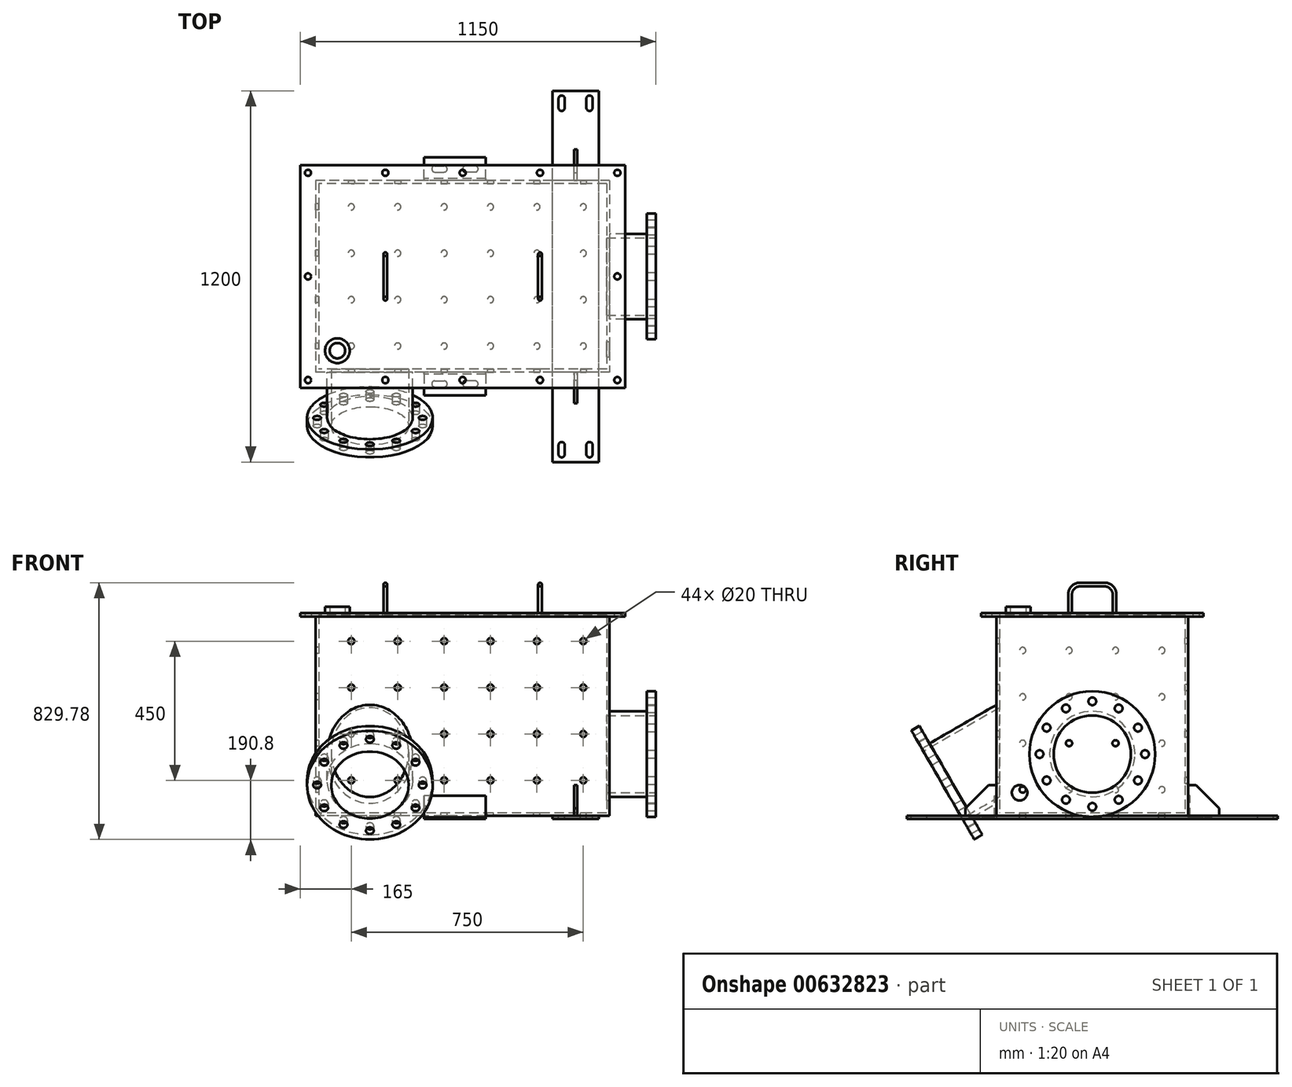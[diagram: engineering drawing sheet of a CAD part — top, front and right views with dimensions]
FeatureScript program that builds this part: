
annotation { "Feature Type Name" : "Feature", "Feature Type Description" : "" }
export const myFeature = defineFeature(function(context is Context, id is Id, definition is map)
    precondition{}
    {
        {
            var Q0;
            Q0=qCreatedBy(makeId("Top.planeOp"),FACE);
            var sketch = newSketch(context, id + "F0", { "sketchPlane" : qUnion([Q0])});
            skLineSegment(sketch, "E0.bottom", {"start": v(475, 310) * mm, "end": v(-475, 310) * mm});
            skLineSegment(sketch, "E0.top", {"start": v(475, -310) * mm, "end": v(-475, -310) * mm});
            skLineSegment(sketch, "E0.left", {"start": v(475, 310) * mm, "end": v(475, -310) * mm});
            skLineSegment(sketch, "E0.right", {"start": v(-475, 310) * mm, "end": v(-475, -310) * mm});
            skPoint(sketch, "E0.middle", {"position": v(0, 0) * mm});
            skSolve(sketch);
        }
        {
            var Q0;
            Q0=makeQuery(id+"F0.imprint","IMPRINT",FACE,{"disambiguationData":[TD([[makeQuery(id+"F0.imprint","IMPRINT",EDGE,{"derivedFrom":sQuery(id+"F0.wireOp",EDGE,"E0.bottom")}),1.0]])]});
            extrude(context, id + "F1", {"entities" : qUnion([Q0]), "depth" : 650 * mm, "offsetDistance" : 25 * mm});
        }
        {
            var Q0;
            Q0=makeQuery(id+"F1.opExtrude","CAP_FACE",FACE,{"disambiguationData":[OSD([sQuery(id+"F0.wireOp",EDGE,"E0.bottom"),sQuery(id+"F0.wireOp",EDGE,"E0.top"),sQuery(id+"F0.wireOp",EDGE,"E0.left"),sQuery(id+"F0.wireOp",EDGE,"E0.right")])],"isStart":false});
            var Q1;
            Q1=makeQuery(id+"F1.opExtrude","SWEPT_BODY",BODY,{"disambiguationData":[OSD([sQuery(id+"F0.wireOp",EDGE,"E0.bottom"),sQuery(id+"F0.wireOp",EDGE,"E0.top"),sQuery(id+"F0.wireOp",EDGE,"E0.left"),sQuery(id+"F0.wireOp",EDGE,"E0.right")])]});
            shell(context, id + "F2", {"entities" : qUnion([Q0]), "parts" : qUnion([Q1]), "thickness" : 10 * mm});
        }
        {
            var Q0;
            Q0=makeQuery(id+"F1.opExtrude","SWEPT_FACE",FACE,{"disambiguationData":[OSD([sQuery(id+"F0.wireOp",EDGE,"E0.left")])]});
            var sketch = newSketch(context, id + "F3", { "sketchPlane" : qUnion([Q0])});
            skCircle(sketch, "E1", {"center": v(0, 200) * mm, "radius": 125 * mm});
            skLineSegment(sketch, "E2", {"start": v(0, 0) * mm, "end": v(0, 200) * mm, "construction": true});
            skSolve(sketch);
        }
        {
            var Q0;
            Q0=sQuery(id+"F3.wireOp",VERTEX,"E1.center");
            var Q1;
            Q1=makeQuery(id+"F1.opExtrude","SWEPT_BODY",BODY,{"disambiguationData":[OSD([sQuery(id+"F0.wireOp",EDGE,"E0.bottom"),sQuery(id+"F0.wireOp",EDGE,"E0.top"),sQuery(id+"F0.wireOp",EDGE,"E0.left"),sQuery(id+"F0.wireOp",EDGE,"E0.right")])]});
            hole(context, id + "F4", {"style" : HoleStyle.SIMPLE, "endStyle" : HoleEndStyle.BLIND, "holeDiameter" : 250 * mm, "majorDiameter" : 5 * mm, "holeDepth" : 200 * mm, "isTappedThrough" : true, "tappedDepth" : 12 * mm, "tapClearance" : 3, "locations" : qUnion([Q0]), "scope" : qUnion([Q1])});
        }
        {
            var Q0;
            Q0=makeQuery(id+"F1.opExtrude","SWEPT_FACE",FACE,{"disambiguationData":[OSD([sQuery(id+"F0.wireOp",EDGE,"E0.top")])]});
            var sketch = newSketch(context, id + "F5", { "sketchPlane" : qUnion([Q0])});
            skCircle(sketch, "E3", {"center": v(-300, 200) * mm, "radius": 125 * mm});
            skLineSegment(sketch, "E4", {"start": v(-425, 200) * mm, "end": v(-175, 200) * mm, "construction": true});
            skSolve(sketch);
        }
        {
            var Q0;
            Q0=makeQuery(id+"F1.opExtrude","CAP_FACE",FACE,{"disambiguationData":[OSD([sQuery(id+"F0.wireOp",EDGE,"E0.bottom"),sQuery(id+"F0.wireOp",EDGE,"E0.top"),sQuery(id+"F0.wireOp",EDGE,"E0.left"),sQuery(id+"F0.wireOp",EDGE,"E0.right")])],"isStart":false});
            var sketch = newSketch(context, id + "F6", { "sketchPlane" : qUnion([Q0])});
            skLineSegment(sketch, "E5.bottom", {"start": v(475, 310) * mm, "end": v(-475, 310) * mm});
            skLineSegment(sketch, "E5.top", {"start": v(475, -310) * mm, "end": v(-475, -310) * mm});
            skLineSegment(sketch, "E5.left", {"start": v(475, 310) * mm, "end": v(475, -310) * mm});
            skLineSegment(sketch, "E5.right", {"start": v(-475, 310) * mm, "end": v(-475, -310) * mm});
            skPoint(sketch, "E5.middle", {"position": v(0, 0) * mm});
            skLineSegment(sketch, "E6.bottom", {"start": v(525, 360) * mm, "end": v(-525, 360) * mm});
            skLineSegment(sketch, "E6.top", {"start": v(525, -360) * mm, "end": v(-525, -360) * mm});
            skLineSegment(sketch, "E6.left", {"start": v(525, 360) * mm, "end": v(525, -360) * mm});
            skLineSegment(sketch, "E6.right", {"start": v(-525, 360) * mm, "end": v(-525, -360) * mm});
            skSolve(sketch);
        }
        {
            var Q0;
            Q0=makeQuery(id+"F6.imprint","IMPRINT",FACE,{"disambiguationData":[TD([[makeQuery(id+"F6.imprint","IMPRINT",EDGE,{"derivedFrom":sQuery(id+"F6.wireOp",EDGE,"E5.bottom")}),-1.0]])]});
            var sketch = newSketch(context, id + "F7", { "sketchPlane" : qUnion([Q0])});
            skCircle(sketch, "E7", {"center": v(-500, 335) * mm, "radius": 10 * mm});
            skCircle(sketch, "E8.MirrorC", {"center": v(500, 335) * mm, "radius": 10 * mm});
            skCircle(sketch, "E9", {"center": v(0, 335) * mm, "radius": 10 * mm});
            skCircle(sketch, "E10", {"center": v(250, 335) * mm, "radius": 10 * mm});
            skCircle(sketch, "E11", {"center": v(-250, 335) * mm, "radius": 10 * mm});
            skCircle(sketch, "E12", {"center": v(-500, 0) * mm, "radius": 10 * mm});
            skCircle(sketch, "E13", {"center": v(500, 0) * mm, "radius": 10 * mm});
            skCircle(sketch, "E14.MirrorC", {"center": v(-250, -335) * mm, "radius": 10 * mm});
            skCircle(sketch, "E15.MirrorC", {"center": v(0, -335) * mm, "radius": 10 * mm});
            skCircle(sketch, "E16.MirrorC", {"center": v(250, -335) * mm, "radius": 10 * mm});
            skCircle(sketch, "E17.MirrorC", {"center": v(500, -335) * mm, "radius": 10 * mm});
            skCircle(sketch, "E18.MirrorC", {"center": v(-500, -335) * mm, "radius": 10 * mm});
            skSolve(sketch);
        }
        {
            var Q0;
            Q0=makeQuery(id+"FEyW0m5oHBMubmV_1.boolean.opBoolean","MERGE",FACE,{"derivedFrom":[makeQuery(id+"Fs8Oh72M1rwnpf4_1.boolean.opBoolean","MERGE",FACE,{"derivedFrom":[makeQuery(id+"F1.opExtrude","SWEPT_FACE",FACE,{"disambiguationData":[OSD([sQuery(id+"F0.wireOp",EDGE,"E0.left")])]}),makeQuery(id+"Fs8Oh72M1rwnpf4_1.opExtrude","SWEPT_FACE",FACE,{"disambiguationData":[OSD([sQuery(id+"F4QqQAWiacnO0fX_1.wireOp",EDGE,"CHtHYlyW-yg5j-FexC-awxB-8z9hYpKb7upd.right")])]})]}),makeQuery(id+"FEyW0m5oHBMubmV_1.opExtrude","SWEPT_FACE",FACE,{"disambiguationData":[OSD([sQuery(id+"F0J5bgxU2wIGMiN_1.wireOp",EDGE,"msL39oIi-AbLE-4iKB-2RcJ-U97ccpWqk1Ai.left")])]})]});
            var sketch = newSketch(context, id + "F8", { "sketchPlane" : qUnion([Q0])});
            skCircle(sketch, "E19", {"center": v(0, 200) * mm, "radius": 138 * mm});
            skSolve(sketch);
        }
        {
            var Q0;
            Q0=makeQuery(id+"F8.imprint","IMPRINT",FACE,{"disambiguationData":[TD([[makeQuery(id+"F8.imprint","IMPRINT",EDGE,{"derivedFrom":sQuery(id+"F8.wireOp",EDGE,"E19")}),1.0]])]});
            extrude(context, id + "F9", {"entities" : qUnion([Q0]), "operationType" : NewBodyOperationType.ADD, "depth" : 150 * mm, "offsetDistance" : 25 * mm});
        }
        {
            var Q0;
            Q0=makeQuery(id+"F9.opExtrude","CAP_FACE",FACE,{"disambiguationData":[OSD([sQuery(id+"F4.hole-0.sketch.wireOp",EDGE,"core_line_2"),sQuery(id+"F4.hole-0.sketch.wireOp",EDGE,"core_line_3"),sQuery(id+"F8.wireOp",EDGE,"E19")])],"isStart":false});
            var sketch = newSketch(context, id + "F10", { "sketchPlane" : qUnion([Q0])});
            skCircle(sketch, "E20", {"center": v(0, 200) * mm, "radius": 203 * mm});
            skCircle(sketch, "E21", {"center": v(0, 370.5) * mm, "radius": 12.5 * mm});
            skCircle(sketch, "E22.1.0", {"center": v(-85.25, 347.66) * mm, "radius": 12.5 * mm});
            skCircle(sketch, "E22.2.0", {"center": v(-147.66, 285.25) * mm, "radius": 12.5 * mm});
            skCircle(sketch, "E22.3.0", {"center": v(-170.5, 200) * mm, "radius": 12.5 * mm});
            skCircle(sketch, "E22.4.0", {"center": v(-147.66, 114.75) * mm, "radius": 12.5 * mm});
            skCircle(sketch, "E22.5.0", {"center": v(-85.25, 52.34) * mm, "radius": 12.5 * mm});
            skCircle(sketch, "E22.6.0", {"center": v(0, 29.5) * mm, "radius": 12.5 * mm});
            skCircle(sketch, "E22.7.0", {"center": v(85.25, 52.34) * mm, "radius": 12.5 * mm});
            skCircle(sketch, "E22.8.0", {"center": v(147.66, 114.75) * mm, "radius": 12.5 * mm});
            skCircle(sketch, "E22.9.0", {"center": v(170.5, 200) * mm, "radius": 12.5 * mm});
            skCircle(sketch, "E22.10.0", {"center": v(147.66, 285.25) * mm, "radius": 12.5 * mm});
            skCircle(sketch, "E22.11.0", {"center": v(85.25, 347.66) * mm, "radius": 12.5 * mm});
            skCircle(sketch, "E23", {"center": v(0, 200) * mm, "radius": 170.5 * mm, "construction": true});
            skSolve(sketch);
        }
        {
            var Q0;
            Q0=makeQuery(id+"F10.imprint","IMPRINT",FACE,{"disambiguationData":[TD([[makeQuery(id+"F10.imprint","IMPRINT",EDGE,{"derivedFrom":sQuery(id+"F10.wireOp",EDGE,"E20")}),1.0]])]});
            extrude(context, id + "F11", {"entities" : qUnion([Q0]), "operationType" : NewBodyOperationType.ADD, "oppositeDirection" : true, "depth" : 30 * mm, "hasOffset" : true, "offsetDistance" : 30 * mm});
        }
        {
            var Q0;
            Q0=makeQuery(id+"FEyW0m5oHBMubmV_1.boolean.opBoolean","MERGE",FACE,{"derivedFrom":[makeQuery(id+"Fs8Oh72M1rwnpf4_1.boolean.opBoolean","MERGE",FACE,{"derivedFrom":[makeQuery(id+"F1.opExtrude","SWEPT_FACE",FACE,{"disambiguationData":[OSD([sQuery(id+"F0.wireOp",EDGE,"E0.right")])]}),makeQuery(id+"Fs8Oh72M1rwnpf4_1.opExtrude","SWEPT_FACE",FACE,{"disambiguationData":[OSD([sQuery(id+"F4QqQAWiacnO0fX_1.wireOp",EDGE,"CHtHYlyW-yg5j-FexC-awxB-8z9hYpKb7upd.left")])]})]}),makeQuery(id+"FEyW0m5oHBMubmV_1.opExtrude","SWEPT_FACE",FACE,{"disambiguationData":[OSD([sQuery(id+"F0J5bgxU2wIGMiN_1.wireOp",EDGE,"msL39oIi-AbLE-4iKB-2RcJ-U97ccpWqk1Ai.right")])]})]});
            var sketch = newSketch(context, id + "F12", { "sketchPlane" : qUnion([Q0])});
            skLineSegment(sketch, "E24", {"start": v(-310, 65) * mm, "end": v(-310, -10) * mm});
            skLineSegment(sketch, "E25", {"start": v(-310, -10) * mm, "end": v(-385, -10) * mm});
            skLineSegment(sketch, "E26", {"start": v(-316, -4) * mm, "end": v(-316, 65) * mm});
            skLineSegment(sketch, "E27", {"start": v(-316, 65) * mm, "end": v(-310, 65) * mm});
            skLineSegment(sketch, "E28", {"start": v(-316, -4) * mm, "end": v(-385, -4) * mm});
            skLineSegment(sketch, "E29", {"start": v(-385, -4) * mm, "end": v(-385, -10) * mm});
            skLineSegment(sketch, "E30.MirrorCS", {"start": v(385, -4) * mm, "end": v(385, -10) * mm});
            skLineSegment(sketch, "E31.MirrorCS", {"start": v(316, 65) * mm, "end": v(310, 65) * mm});
            skLineSegment(sketch, "E32.MirrorCS", {"start": v(316, -4) * mm, "end": v(316, 65) * mm});
            skLineSegment(sketch, "E33.MirrorCS", {"start": v(310, 65) * mm, "end": v(310, -10) * mm});
            skLineSegment(sketch, "E34.MirrorCS", {"start": v(316, -4) * mm, "end": v(385, -4) * mm});
            skLineSegment(sketch, "E35.MirrorCS", {"start": v(310, -10) * mm, "end": v(385, -10) * mm});
            skSolve(sketch);
        }
        {
            var Q0;
            Q0 = qSketchRegion(id + "F12", true);
            var Q1;
            Q1 = qSketchRegion(id + "Fb1wKp0skmJjsFw_1", true);
            extrude(context, id + "F13", {"entities" : qUnion([Q0, Q1]), "operationType" : NewBodyOperationType.ADD, "oppositeDirection" : true, "depth" : 550 * mm, "offsetDistance" : 25 * mm, "hasSecondDirection" : true, "secondDirectionOppositeDirection" : true, "secondDirectionDepth" : 350 * mm});
        }
        {
            var Q0;
            Q0=makeQuery(id+"F13.opExtrude","SWEPT_FACE",FACE,{"disambiguationData":[OSD([sQuery(id+"F12.wireOp",EDGE,"E35.MirrorCS")])]});
            var sketch = newSketch(context, id + "F14", { "sketchPlane" : qUnion([Q0])});
            skArc(sketch, "E36", {"start": v(-90, 357.5) * mm, "mid": v(-100, 347.5) * mm, "end": v(-90, 337.5) * mm});
            skArc(sketch, "E37.MirrorCS", {"start": v(-60, 357.5) * mm, "mid": v(-50, 347.5) * mm, "end": v(-60, 337.5) * mm});
            skLineSegment(sketch, "E38", {"start": v(-25, 385) * mm, "end": v(-25, 310) * mm});
            skLineSegment(sketch, "E39", {"start": v(-90, 357.5) * mm, "end": v(-60, 357.5) * mm});
            skLineSegment(sketch, "E40", {"start": v(-90, 337.5) * mm, "end": v(-60, 337.5) * mm});
            skLineSegment(sketch, "E41.MirrorCS", {"start": v(40, 357.5) * mm, "end": v(10, 357.5) * mm});
            skArc(sketch, "E42.MirrorCS", {"start": v(40, 357.5) * mm, "mid": v(50, 347.5) * mm, "end": v(40, 337.5) * mm});
            skLineSegment(sketch, "E43.MirrorCS", {"start": v(40, 337.5) * mm, "end": v(10, 337.5) * mm});
            skArc(sketch, "E44.MirrorCS", {"start": v(10, 357.5) * mm, "mid": v(0, 347.5) * mm, "end": v(10, 337.5) * mm});
            skLineSegment(sketch, "E45.MirrorCS", {"start": v(40, -357.5) * mm, "end": v(10, -357.5) * mm});
            skArc(sketch, "E46.MirrorCS", {"start": v(40, -357.5) * mm, "mid": v(50, -347.5) * mm, "end": v(40, -337.5) * mm});
            skLineSegment(sketch, "E47.MirrorCS", {"start": v(40, -337.5) * mm, "end": v(10, -337.5) * mm});
            skArc(sketch, "E48.MirrorCS", {"start": v(10, -357.5) * mm, "mid": v(0, -347.5) * mm, "end": v(10, -337.5) * mm});
            skArc(sketch, "E49.MirrorCS", {"start": v(-60, -357.5) * mm, "mid": v(-50, -347.5) * mm, "end": v(-60, -337.5) * mm});
            skLineSegment(sketch, "E50.MirrorCS", {"start": v(-90, -337.5) * mm, "end": v(-60, -337.5) * mm});
            skArc(sketch, "E51.MirrorCS", {"start": v(-90, -357.5) * mm, "mid": v(-100, -347.5) * mm, "end": v(-90, -337.5) * mm});
            skLineSegment(sketch, "E52.MirrorCS", {"start": v(-90, -357.5) * mm, "end": v(-60, -357.5) * mm});
            skSolve(sketch);
        }
        {
            var Q0;
            Q0 = qSketchRegion(id + "F14", true);
            extrude(context, id + "F15", {"entities" : qUnion([Q0]), "operationType" : NewBodyOperationType.REMOVE, "oppositeDirection" : true, "depth" : 6 * mm, "offsetDistance" : 25 * mm});
        }
        {
            var Q0;
            Q0=makeQuery(id+"F0.imprint","IMPRINT",FACE,{"disambiguationData":[TD([[makeQuery(id+"F0.imprint","IMPRINT",EDGE,{"derivedFrom":sQuery(id+"F0.wireOp",EDGE,"E0.bottom")}),1.0]])]});
            var sketch = newSketch(context, id + "F16", { "sketchPlane" : qUnion([Q0])});
            skLineSegment(sketch, "E53.bottom", {"start": v(290, -600) * mm, "end": v(440, -600) * mm});
            skLineSegment(sketch, "E53.top", {"start": v(290, 600) * mm, "end": v(440, 600) * mm});
            skLineSegment(sketch, "E53.left", {"start": v(290, -600) * mm, "end": v(290, 600) * mm});
            skLineSegment(sketch, "E53.right", {"start": v(440, -600) * mm, "end": v(440, 600) * mm});
            skArc(sketch, "E54.MirrorCS", {"start": v(420, -575) * mm, "mid": v(410, -585) * mm, "end": v(400, -575) * mm});
            skLineSegment(sketch, "E55.MirrorCS", {"start": v(420, -575) * mm, "end": v(420, -545) * mm});
            skLineSegment(sketch, "E56.MirrorCS", {"start": v(400, -575) * mm, "end": v(400, -545) * mm});
            skArc(sketch, "E57.MirrorCS", {"start": v(420, -545) * mm, "mid": v(410, -535) * mm, "end": v(400, -545) * mm});
            skArc(sketch, "E58.MirrorCS", {"start": v(420, 575) * mm, "mid": v(410, 585) * mm, "end": v(400, 575) * mm});
            skLineSegment(sketch, "E59.MirrorCS", {"start": v(400, 575) * mm, "end": v(400, 545) * mm});
            skArc(sketch, "E60.MirrorCS", {"start": v(420, 545) * mm, "mid": v(410, 535) * mm, "end": v(400, 545) * mm});
            skLineSegment(sketch, "E61.MirrorCS", {"start": v(420, 575) * mm, "end": v(420, 545) * mm});
            skArc(sketch, "E62.MirrorCS", {"start": v(310, 545) * mm, "mid": v(320, 535) * mm, "end": v(330, 545) * mm});
            skLineSegment(sketch, "E63.MirrorCS", {"start": v(330, 575) * mm, "end": v(330, 545) * mm});
            skLineSegment(sketch, "E64.MirrorCS", {"start": v(310, 575) * mm, "end": v(310, 545) * mm});
            skArc(sketch, "E65.MirrorCS", {"start": v(310, 575) * mm, "mid": v(320, 585) * mm, "end": v(330, 575) * mm});
            skLineSegment(sketch, "E66.MirrorCS", {"start": v(330, -575) * mm, "end": v(330, -545) * mm});
            skLineSegment(sketch, "E67.MirrorCS", {"start": v(310, -575) * mm, "end": v(310, -545) * mm});
            skArc(sketch, "E68.MirrorCS", {"start": v(310, -575) * mm, "mid": v(320, -585) * mm, "end": v(330, -575) * mm});
            skArc(sketch, "E69.MirrorCS", {"start": v(310, -545) * mm, "mid": v(320, -535) * mm, "end": v(330, -545) * mm});
            skSolve(sketch);
        }
        {
            var Q0;
            Q0 = qSketchRegion(id + "F16", true);
            extrude(context, id + "F17", {"entities" : qUnion([Q0]), "operationType" : NewBodyOperationType.ADD, "oppositeDirection" : true, "depth" : 10 * mm, "offsetDistance" : 25 * mm});
        }
        {
            var Q0;
            Q0=makeQuery(id+"F2.opShell","OFFSET_FACE",FACE,{"disambiguationData":[OSD([sQuery(id+"F0.wireOp",EDGE,"E0.bottom"),sQuery(id+"F0.wireOp",EDGE,"E0.top"),sQuery(id+"F0.wireOp",EDGE,"E0.left"),sQuery(id+"F0.wireOp",EDGE,"E0.right")])]});
            var sketch = newSketch(context, id + "F18", { "sketchPlane" : qUnion([Q0])});
            skCircle(sketch, "E70.MirrorC", {"center": v(390, 225) * mm, "radius": 10 * mm});
            skCircle(sketch, "E71.MirrorC", {"center": v(390, 75) * mm, "radius": 10 * mm});
            skCircle(sketch, "E72.MirrorC", {"center": v(240, 225) * mm, "radius": 10 * mm});
            skCircle(sketch, "E73.MirrorC", {"center": v(240, 75) * mm, "radius": 10 * mm});
            skCircle(sketch, "E74.MirrorC", {"center": v(240, -75) * mm, "radius": 10 * mm});
            skCircle(sketch, "E75.MirrorC", {"center": v(390, -75) * mm, "radius": 10 * mm});
            skCircle(sketch, "E76.MirrorC", {"center": v(240, -225) * mm, "radius": 10 * mm});
            skCircle(sketch, "E77.MirrorC", {"center": v(390, -225) * mm, "radius": 10 * mm});
            skCircle(sketch, "E78.MirrorC", {"center": v(90, 75) * mm, "radius": 10 * mm});
            skCircle(sketch, "E79.MirrorC", {"center": v(-60, 75) * mm, "radius": 10 * mm});
            skCircle(sketch, "E80.MirrorC", {"center": v(90, 225) * mm, "radius": 10 * mm});
            skCircle(sketch, "E81.MirrorC", {"center": v(-60, 225) * mm, "radius": 10 * mm});
            skCircle(sketch, "E82.MirrorC", {"center": v(90, -75) * mm, "radius": 10 * mm});
            skCircle(sketch, "E83.MirrorC", {"center": v(90, -225) * mm, "radius": 10 * mm});
            skCircle(sketch, "E84.MirrorC", {"center": v(-60, -225) * mm, "radius": 10 * mm});
            skCircle(sketch, "E85.MirrorC", {"center": v(-60, -75) * mm, "radius": 10 * mm});
            skCircle(sketch, "E86.MirrorC", {"center": v(-210, 75) * mm, "radius": 10 * mm});
            skCircle(sketch, "E87.MirrorC", {"center": v(-210, -75) * mm, "radius": 10 * mm});
            skCircle(sketch, "E88.MirrorC", {"center": v(-210, -225) * mm, "radius": 10 * mm});
            skCircle(sketch, "E89.MirrorC", {"center": v(-210, 225) * mm, "radius": 10 * mm});
            skCircle(sketch, "E90.MirrorC", {"center": v(-360, 225) * mm, "radius": 10 * mm});
            skCircle(sketch, "E91.MirrorC", {"center": v(-360, 75) * mm, "radius": 10 * mm});
            skCircle(sketch, "E92.MirrorC", {"center": v(-360, -75) * mm, "radius": 10 * mm});
            skCircle(sketch, "E93.MirrorC", {"center": v(-360, -225) * mm, "radius": 10 * mm});
            skSolve(sketch);
        }
        {
            var Q0;
            Q0 = qSketchRegion(id + "F18", true);
            var Q1;
            Q1=makeQuery(id+"F17.opExtrude","CAP_FACE",FACE,{"disambiguationData":[OSD([sQuery(id+"F16.wireOp",EDGE,"E53.bottom"),sQuery(id+"F16.wireOp",EDGE,"E53.top"),sQuery(id+"F16.wireOp",EDGE,"E53.left"),sQuery(id+"F16.wireOp",EDGE,"E53.right"),sQuery(id+"F16.wireOp",EDGE,"E54.MirrorCS"),sQuery(id+"F16.wireOp",EDGE,"E55.MirrorCS"),sQuery(id+"F16.wireOp",EDGE,"E56.MirrorCS"),sQuery(id+"F16.wireOp",EDGE,"E57.MirrorCS"),sQuery(id+"F16.wireOp",EDGE,"E58.MirrorCS"),sQuery(id+"F16.wireOp",EDGE,"E59.MirrorCS"),sQuery(id+"F16.wireOp",EDGE,"E60.MirrorCS"),sQuery(id+"F16.wireOp",EDGE,"E61.MirrorCS"),sQuery(id+"F16.wireOp",EDGE,"E62.MirrorCS"),sQuery(id+"F16.wireOp",EDGE,"E63.MirrorCS"),sQuery(id+"F16.wireOp",EDGE,"E64.MirrorCS"),sQuery(id+"F16.wireOp",EDGE,"E65.MirrorCS"),sQuery(id+"F16.wireOp",EDGE,"E66.MirrorCS"),sQuery(id+"F16.wireOp",EDGE,"E67.MirrorCS"),sQuery(id+"F16.wireOp",EDGE,"E68.MirrorCS"),sQuery(id+"F16.wireOp",EDGE,"E69.MirrorCS")])],"isStart":false});
            extrude(context, id + "F19", {"entities" : qUnion([Q0, Q1]), "operationType" : NewBodyOperationType.REMOVE, "oppositeDirection" : true, "depth" : 20 * mm, "offsetDistance" : 25 * mm});
        }
        {
            var Q0;
            Q0=makeQuery(id+"F1.opExtrude","SWEPT_FACE",FACE,{"disambiguationData":[OSD([sQuery(id+"F0.wireOp",EDGE,"E0.top")])]});
            var sketch = newSketch(context, id + "F20", { "sketchPlane" : qUnion([Q0])});
            skLineSegment(sketch, "E94", {"start": v(465, 610) * mm, "end": v(465, 40) * mm, "construction": true});
            skLineSegment(sketch, "E95", {"start": v(315, 610) * mm, "end": v(315, 40) * mm, "construction": true});
            skLineSegment(sketch, "E96", {"start": v(15, 610) * mm, "end": v(15, 40) * mm, "construction": true});
            skLineSegment(sketch, "E97", {"start": v(-135, 10) * mm, "end": v(-135, 610) * mm, "construction": true});
            skLineSegment(sketch, "E98", {"start": v(465, 640) * mm, "end": v(-135, 640) * mm, "construction": true});
            skCircle(sketch, "E99", {"center": v(390, 115) * mm, "radius": 10 * mm});
            skCircle(sketch, "E100.MirrorC", {"center": v(390, 265) * mm, "radius": 10 * mm});
            skCircle(sketch, "E101.MirrorC", {"center": v(390, 415) * mm, "radius": 10 * mm});
            skCircle(sketch, "E102.MirrorC", {"center": v(390, 565) * mm, "radius": 10 * mm});
            skCircle(sketch, "E103.MirrorC", {"center": v(240, 265) * mm, "radius": 10 * mm});
            skCircle(sketch, "E104.MirrorC", {"center": v(240, 115) * mm, "radius": 10 * mm});
            skCircle(sketch, "E105.MirrorC", {"center": v(240, 415) * mm, "radius": 10 * mm});
            skCircle(sketch, "E106.MirrorC", {"center": v(240, 565) * mm, "radius": 10 * mm});
            skLineSegment(sketch, "E107", {"start": v(165, 640) * mm, "end": v(165, 40) * mm, "construction": true});
            skCircle(sketch, "E108.MirrorC", {"center": v(90, 565) * mm, "radius": 10 * mm});
            skCircle(sketch, "E109.MirrorC", {"center": v(-60, 565) * mm, "radius": 10 * mm});
            skCircle(sketch, "E110.MirrorC", {"center": v(90, 415) * mm, "radius": 10 * mm});
            skCircle(sketch, "E111.MirrorC", {"center": v(-60, 415) * mm, "radius": 10 * mm});
            skCircle(sketch, "E112.MirrorC", {"center": v(-60, 265) * mm, "radius": 10 * mm});
            skCircle(sketch, "E113.MirrorC", {"center": v(90, 265) * mm, "radius": 10 * mm});
            skCircle(sketch, "E114.MirrorC", {"center": v(-60, 115) * mm, "radius": 10 * mm});
            skCircle(sketch, "E115.MirrorC", {"center": v(90, 115) * mm, "radius": 10 * mm});
            skLineSegment(sketch, "E116", {"start": v(15, 490) * mm, "end": v(315, 490) * mm, "construction": true});
            skLineSegment(sketch, "E117", {"start": v(15, 190) * mm, "end": v(315, 190) * mm, "construction": true});
            skLineSegment(sketch, "E118", {"start": v(315, 340) * mm, "end": v(465, 340) * mm, "construction": true});
            skLineSegment(sketch, "E119", {"start": v(-135, 340) * mm, "end": v(15, 340) * mm, "construction": true});
            skCircle(sketch, "E120.MirrorC", {"center": v(-210, 565) * mm, "radius": 10 * mm});
            skCircle(sketch, "E121.MirrorC", {"center": v(-360, 565) * mm, "radius": 10 * mm});
            skCircle(sketch, "E122.MirrorC", {"center": v(-360, 415) * mm, "radius": 10 * mm});
            skCircle(sketch, "E123.MirrorC", {"center": v(-210, 415) * mm, "radius": 10 * mm});
            skSolve(sketch);
        }
        {
            var Q0;
            Q0 = qSketchRegion(id + "F20", true);
            extrude(context, id + "F21", {"entities" : qUnion([Q0]), "operationType" : NewBodyOperationType.REMOVE, "endBound" : BoundingType.THROUGH_ALL, "oppositeDirection" : true, "depth" : 25 * mm, "offsetDistance" : 25 * mm});
        }
        {
            var Q0;
            Q0=makeQuery(id+"F1.opExtrude","SWEPT_FACE",FACE,{"disambiguationData":[OSD([sQuery(id+"F0.wireOp",EDGE,"E0.bottom")])]});
            var sketch = newSketch(context, id + "F22", { "sketchPlane" : qUnion([Q0])});
            skLineSegment(sketch, "E124", {"start": v(210, 415) * mm, "end": v(210, 23.45) * mm, "construction": true});
            skLineSegment(sketch, "E125", {"start": v(60, 265) * mm, "end": v(475, 265) * mm, "construction": true});
            skLineSegment(sketch, "E126", {"start": v(60, 115) * mm, "end": v(446.72, 115) * mm, "construction": true});
            skLineSegment(sketch, "E127", {"start": v(360, 415) * mm, "end": v(360, 23.45) * mm, "construction": true});
            skCircle(sketch, "E128", {"center": v(210, 265) * mm, "radius": 10 * mm});
            skCircle(sketch, "E129", {"center": v(360, 265) * mm, "radius": 10 * mm});
            skCircle(sketch, "E130", {"center": v(210, 115) * mm, "radius": 10 * mm});
            skCircle(sketch, "E131", {"center": v(360, 115) * mm, "radius": 10 * mm});
            skSolve(sketch);
        }
        {
            var Q0;
            Q0 = qSketchRegion(id + "F22", true);
            extrude(context, id + "F23", {"entities" : qUnion([Q0]), "operationType" : NewBodyOperationType.REMOVE, "oppositeDirection" : true, "depth" : 25 * mm, "offsetDistance" : 25 * mm});
        }
        {
            var Q0;
            Q0=makeQuery(id+"F17.opExtrude","SWEPT_FACE",FACE,{"disambiguationData":[OSD([sQuery(id+"F16.wireOp",EDGE,"E53.right")])]});
            var sketch = newSketch(context, id + "F24", { "sketchPlane" : qUnion([Q0])});
            skLineSegment(sketch, "E132", {"start": v(-310, 0) * mm, "end": v(-310, 100) * mm});
            skLineSegment(sketch, "E133", {"start": v(-310, 100) * mm, "end": v(-335, 100) * mm});
            skLineSegment(sketch, "E134", {"start": v(-335, 100) * mm, "end": v(-410, 25) * mm});
            skLineSegment(sketch, "E135", {"start": v(-410, 25) * mm, "end": v(-410, 0) * mm});
            skLineSegment(sketch, "E136", {"start": v(-410, 0) * mm, "end": v(-310, 0) * mm});
            skLineSegment(sketch, "E137.MirrorCS", {"start": v(310, 100) * mm, "end": v(335, 100) * mm});
            skLineSegment(sketch, "E138.MirrorCS", {"start": v(335, 100) * mm, "end": v(410, 25) * mm});
            skLineSegment(sketch, "E139.MirrorCS", {"start": v(410, 25) * mm, "end": v(410, 0) * mm});
            skLineSegment(sketch, "E140.MirrorCS", {"start": v(410, 0) * mm, "end": v(310, 0) * mm});
            skLineSegment(sketch, "E141.MirrorCS", {"start": v(310, 0) * mm, "end": v(310, 100) * mm});
            skSolve(sketch);
        }
        {
            var Q0;
            Q0 = qSketchRegion(id + "F24", true);
            extrude(context, id + "F25", {"entities" : qUnion([Q0]), "operationType" : NewBodyOperationType.ADD, "oppositeDirection" : true, "depth" : 80 * mm, "offsetDistance" : 25 * mm, "hasSecondDirection" : true, "secondDirectionOppositeDirection" : true, "secondDirectionDepth" : 70 * mm});
        }
        {
            var Q0;
            Q0=sQuery(id+"F5.wireOp",EDGE,"E4");
            cPlane(context, id + "F26", {"entities" : qUnion([Q0]), "cplaneType" : CPlaneType.LINE_ANGLE, "offset" : 25 * mm, "angle" : 30 * degree, "width" : 150 * mm, "height" : 150 * mm});
        }
        {
            var Q0;
            Q0=qCreatedBy(id+"F26.planeOp",FACE);
            var sketch = newSketch(context, id + "F27", { "sketchPlane" : qUnion([Q0])});
            skCircle(sketch, "E142", {"center": v(300, 328.2) * mm, "radius": 138 * mm});
            skSolve(sketch);
        }
        {
            var Q0;
            Q0 = qSketchRegion(id + "F27", true);
            var Q1;
            Q1=makeQuery(id+"F1.opExtrude","SWEPT_FACE",FACE,{"disambiguationData":[OSD([sQuery(id+"F0.wireOp",EDGE,"E0.top")])]});
            extrude(context, id + "F28", {"entities" : qUnion([Q0]), "operationType" : NewBodyOperationType.ADD, "oppositeDirection" : true, "depth" : 200 * mm, "offsetDistance" : 25 * mm, "hasSecondDirection" : true, "secondDirectionBound" : SecondDirectionBoundingType.UP_TO_SURFACE, "secondDirectionOppositeDirection" : false, "secondDirectionDepth" : 25 * mm, "secondDirectionBoundEntityFace" : qUnion([Q1])});
        }
        {
            var Q0;
            Q0=makeQuery(id+"F28.opExtrude","CAP_FACE",FACE,{"disambiguationData":[OSD([sQuery(id+"F27.wireOp",EDGE,"E142")])],"isStart":false});
            var sketch = newSketch(context, id + "F29", { "sketchPlane" : qUnion([Q0])});
            skCircle(sketch, "E143", {"center": v(-300, 328.2) * mm, "radius": 125 * mm});
            skSolve(sketch);
        }
        {
            var Q0;
            Q0 = qSketchRegion(id + "F29", true);
            var Q1;
            Q1=makeQuery(id+"F2.opShell","OFFSET_FACE",FACE,{"disambiguationData":[OSD([sQuery(id+"F0.wireOp",EDGE,"E0.top")])]});
            extrude(context, id + "F30", {"entities" : qUnion([Q0]), "operationType" : NewBodyOperationType.REMOVE, "endBound" : BoundingType.UP_TO_SURFACE, "oppositeDirection" : true, "depth" : 250 * mm, "endBoundEntityFace" : qUnion([Q1]), "offsetDistance" : 25 * mm});
        }
        {
            var Q0;
            Q0=makeQuery(id+"F28.opExtrude","CAP_FACE",FACE,{"disambiguationData":[OSD([sQuery(id+"F27.wireOp",EDGE,"E142")])],"isStart":false});
            var sketch = newSketch(context, id + "F31", { "sketchPlane" : qUnion([Q0])});
            skCircle(sketch, "E144", {"center": v(-300, 328.2) * mm, "radius": 203 * mm});
            skCircle(sketch, "E145", {"center": v(-300, 498.7) * mm, "radius": 12.5 * mm});
            skPoint(sketch, "E146.center", {"position": v(-300, 302.7) * mm});
            skCircle(sketch, "E147", {"center": v(-300, 328.2) * mm, "radius": 138 * mm});
            skCircle(sketch, "E148", {"center": v(-300, 328.2) * mm, "radius": 170.5 * mm, "construction": true});
            skCircle(sketch, "E149.1.0", {"center": v(-385.25, 475.86) * mm, "radius": 12.5 * mm});
            skPoint(sketch, "E149.1.1", {"position": v(-287.25, 306.12) * mm});
            skCircle(sketch, "E149.2.0", {"center": v(-447.66, 413.46) * mm, "radius": 12.5 * mm});
            skPoint(sketch, "E149.2.1", {"position": v(-277.91, 315.45) * mm});
            skCircle(sketch, "E149.3.0", {"center": v(-470.5, 328.2) * mm, "radius": 12.5 * mm});
            skPoint(sketch, "E149.3.1", {"position": v(-274.5, 328.2) * mm});
            skCircle(sketch, "E149.4.0", {"center": v(-447.66, 242.96) * mm, "radius": 12.5 * mm});
            skPoint(sketch, "E149.4.1", {"position": v(-277.91, 340.96) * mm});
            skCircle(sketch, "E149.5.0", {"center": v(-385.25, 180.55) * mm, "radius": 12.5 * mm});
            skPoint(sketch, "E149.5.1", {"position": v(-287.25, 350.3) * mm});
            skCircle(sketch, "E149.6.0", {"center": v(-300, 157.7) * mm, "radius": 12.5 * mm});
            skPoint(sketch, "E149.6.1", {"position": v(-300, 353.71) * mm});
            skCircle(sketch, "E149.7.0", {"center": v(-214.75, 180.55) * mm, "radius": 12.5 * mm});
            skPoint(sketch, "E149.7.1", {"position": v(-312.75, 350.3) * mm});
            skCircle(sketch, "E149.8.0", {"center": v(-152.34, 242.96) * mm, "radius": 12.5 * mm});
            skPoint(sketch, "E149.8.1", {"position": v(-322.09, 340.96) * mm});
            skCircle(sketch, "E149.9.0", {"center": v(-129.5, 328.2) * mm, "radius": 12.5 * mm});
            skPoint(sketch, "E149.9.1", {"position": v(-325.5, 328.2) * mm});
            skCircle(sketch, "E149.10.0", {"center": v(-152.34, 413.46) * mm, "radius": 12.5 * mm});
            skPoint(sketch, "E149.10.1", {"position": v(-322.09, 315.45) * mm});
            skCircle(sketch, "E149.11.0", {"center": v(-214.75, 475.86) * mm, "radius": 12.5 * mm});
            skPoint(sketch, "E149.11.1", {"position": v(-312.75, 306.12) * mm});
            skSolve(sketch);
        }
        {
            var Q0;
            Q0 = qSketchRegion(id + "F31", true);
            extrude(context, id + "F32", {"entities" : qUnion([Q0]), "operationType" : NewBodyOperationType.ADD, "oppositeDirection" : true, "depth" : 30 * mm, "offsetDistance" : 25 * mm});
        }
        {
            var Q0;
            Q0=makeQuery(id+"FFTnacZF29lq5lS_1.boolean.opBoolean","MERGE",FACE,{"derivedFrom":[makeQuery(id+"FOiGVYoEZ6047Ku_1.boolean.opBoolean","MERGE",FACE,{"derivedFrom":[makeQuery(id+"FEyW0m5oHBMubmV_1.boolean.opBoolean","MERGE",FACE,{"derivedFrom":[makeQuery(id+"Fs8Oh72M1rwnpf4_1.boolean.opBoolean","MERGE",FACE,{"derivedFrom":[makeQuery(id+"F1.opExtrude","CAP_FACE",FACE,{"disambiguationData":[OSD([sQuery(id+"F0.wireOp",EDGE,"E0.bottom"),sQuery(id+"F0.wireOp",EDGE,"E0.top"),sQuery(id+"F0.wireOp",EDGE,"E0.left"),sQuery(id+"F0.wireOp",EDGE,"E0.right")])],"isStart":false}),makeQuery(id+"Fs8Oh72M1rwnpf4_1.opExtrude","SWEPT_FACE",FACE,{"disambiguationData":[OSD([sQuery(id+"F4QqQAWiacnO0fX_1.wireOp",EDGE,"CHtHYlyW-yg5j-FexC-awxB-8z9hYpKb7upd.bottom")])]})]}),makeQuery(id+"FEyW0m5oHBMubmV_1.opExtrude","SWEPT_FACE",FACE,{"disambiguationData":[OSD([sQuery(id+"F0J5bgxU2wIGMiN_1.wireOp",EDGE,"msL39oIi-AbLE-4iKB-2RcJ-U97ccpWqk1Ai.bottom")])]})]}),makeQuery(id+"FOiGVYoEZ6047Ku_1.opExtrude","SWEPT_FACE",FACE,{"disambiguationData":[OSD([sQuery(id+"F2uF3QI5gBtSjUF_1.wireOp",EDGE,"tnpDdUtf-ZfiQ-d9Mq-2dJb-kNGGOnwJIISk.bottom")])]})]}),makeQuery(id+"FFTnacZF29lq5lS_1.opExtrude","SWEPT_FACE",FACE,{"disambiguationData":[OSD([sQuery(id+"FnWcgzWaJUUCgpa_1.wireOp",EDGE,"8uEP3YdV-dN8s-lJQq-g5zq-wjJ3foq6nwTj.bottom")])]})]});
            var sketch = newSketch(context, id + "F33", { "sketchPlane" : qUnion([Q0])});
            skLineSegment(sketch, "E150.bottom", {"start": v(-525, 360) * mm, "end": v(525, 360) * mm});
            skLineSegment(sketch, "E150.top", {"start": v(-525, -360) * mm, "end": v(525, -360) * mm});
            skLineSegment(sketch, "E150.left", {"start": v(-525, 360) * mm, "end": v(-525, -360) * mm});
            skLineSegment(sketch, "E150.right", {"start": v(525, 360) * mm, "end": v(525, -360) * mm});
            skCircle(sketch, "E151", {"center": v(-500, 335) * mm, "radius": 10 * mm});
            skCircle(sketch, "E152", {"center": v(-250, 335) * mm, "radius": 10 * mm});
            skCircle(sketch, "E153", {"center": v(0, 335) * mm, "radius": 10 * mm});
            skCircle(sketch, "E154", {"center": v(250, 335) * mm, "radius": 10 * mm});
            skCircle(sketch, "E155", {"center": v(500, 335) * mm, "radius": 10 * mm});
            skCircle(sketch, "E156", {"center": v(500, 0) * mm, "radius": 10 * mm});
            skCircle(sketch, "E157", {"center": v(500, -335) * mm, "radius": 10 * mm});
            skCircle(sketch, "E158", {"center": v(250, -335) * mm, "radius": 10 * mm});
            skCircle(sketch, "E159", {"center": v(0, -335) * mm, "radius": 10 * mm});
            skCircle(sketch, "E160", {"center": v(-250, -335) * mm, "radius": 10 * mm});
            skCircle(sketch, "E161", {"center": v(-500, -335) * mm, "radius": 10 * mm});
            skCircle(sketch, "E162", {"center": v(-500, 0) * mm, "radius": 10 * mm});
            skSolve(sketch);
        }
        {
            var Q0;
            Q0 = qSketchRegion(id + "F33", true);
            extrude(context, id + "F34", {"entities" : qUnion([Q0]), "depth" : 6 * mm, "offsetDistance" : 25 * mm});
        }
        {
            var Q0;
            Q0=makeQuery(id+"F34.opExtrude","CAP_FACE",FACE,{"disambiguationData":[OSD([sQuery(id+"F33.wireOp",EDGE,"E150.bottom"),sQuery(id+"F33.wireOp",EDGE,"E150.top"),sQuery(id+"F33.wireOp",EDGE,"E150.left"),sQuery(id+"F33.wireOp",EDGE,"E150.right"),sQuery(id+"F33.wireOp",EDGE,"E151"),sQuery(id+"F33.wireOp",EDGE,"E152"),sQuery(id+"F33.wireOp",EDGE,"E153"),sQuery(id+"F33.wireOp",EDGE,"E154"),sQuery(id+"F33.wireOp",EDGE,"E155"),sQuery(id+"F33.wireOp",EDGE,"E156"),sQuery(id+"F33.wireOp",EDGE,"E157"),sQuery(id+"F33.wireOp",EDGE,"E158"),sQuery(id+"F33.wireOp",EDGE,"E159"),sQuery(id+"F33.wireOp",EDGE,"E160"),sQuery(id+"F33.wireOp",EDGE,"E161"),sQuery(id+"F33.wireOp",EDGE,"E162")])],"isStart":false});
            var sketch = newSketch(context, id + "F35", { "sketchPlane" : qUnion([Q0])});
            skLineSegment(sketch, "E163", {"start": v(-510, 0) * mm, "end": v(510, 0) * mm, "construction": true});
            skLineSegment(sketch, "E164", {"start": v(-250, 78.02) * mm, "end": v(-250, -71.98) * mm, "construction": true});
            skCircle(sketch, "E165", {"center": v(-250, -71.98) * mm, "radius": 6 * mm});
            skLineSegment(sketch, "E166", {"start": v(0, 0) * mm, "end": v(0, -100.5) * mm, "construction": true});
            skCircle(sketch, "E167.MirrorC", {"center": v(250, -71.98) * mm, "radius": 6 * mm});
            skSolve(sketch);
        }
        {
            var Q0;
            Q0=makeQuery(id+"F34.opExtrude","SWEPT_FACE",FACE,{"disambiguationData":[OSD([sQuery(id+"F33.wireOp",EDGE,"E150.right")])]});
            var sketch = newSketch(context, id + "F36", { "sketchPlane" : qUnion([Q0])});
            skLineSegment(sketch, "E168", {"start": v(-60, 656) * mm, "end": v(-60, 716) * mm});
            skArc(sketch, "E169", {"start": v(-60, 716) * mm, "mid": v(-54.14, 730.14) * mm, "end": v(-40, 736) * mm});
            skPoint(sketch, "E170.endSnap0", {"position": v(0, 656) * mm});
            skLineSegment(sketch, "E171", {"start": v(-40, 736) * mm, "end": v(40, 736) * mm});
            skArc(sketch, "E172", {"start": v(40, 736) * mm, "mid": v(54.14, 730.14) * mm, "end": v(60, 716) * mm});
            skLineSegment(sketch, "E173", {"start": v(60, 716) * mm, "end": v(60, 656) * mm});
            skSolve(sketch);
        }
        {
            var Q0;
            Q0 = qSketchRegion(id + "F35", true);
            var Q1;
            Q1 = qConstructionFilter(qBodyType(qCreatedBy(id + "F36" ,EDGE), BodyType.WIRE), ConstructionObject.NO);
            sweep(context, id + "F37", {"operationType" : NewBodyOperationType.ADD, "profiles" : qUnion([Q0]), "path" : qUnion([Q1])});
        }
        {
            var Q0;
            Q0 = qSketchRegion(id + "F6", true);
            extrude(context, id + "F38", {"entities" : qUnion([Q0]), "operationType" : NewBodyOperationType.ADD, "oppositeDirection" : true, "depth" : 6 * mm, "offsetDistance" : 25 * mm});
        }
        {
            var Q0;
            Q0 = qSketchRegion(id + "F7", true);
            extrude(context, id + "F39", {"entities" : qUnion([Q0]), "operationType" : NewBodyOperationType.REMOVE, "oppositeDirection" : true, "depth" : 6 * mm, "offsetDistance" : 25 * mm});
        }
        {
            var Q0;
            Q0=makeQuery(id+"F1.opExtrude","SWEPT_FACE",FACE,{"disambiguationData":[OSD([sQuery(id+"F0.wireOp",EDGE,"E0.right")])]});
            var sketch = newSketch(context, id + "F40", { "sketchPlane" : qUnion([Q0])});
            skLineSegment(sketch, "E174", {"start": v(0, 644) * mm, "end": v(0, 0) * mm, "construction": true});
            skLineSegment(sketch, "E175", {"start": v(-310, 310) * mm, "end": v(310, 310) * mm, "construction": true});
            skLineSegment(sketch, "E176", {"start": v(-150, 310) * mm, "end": v(-150, 0) * mm, "construction": true});
            skLineSegment(sketch, "E177", {"start": v(-310, 160) * mm, "end": v(0, 160) * mm, "construction": true});
            skCircle(sketch, "E178", {"center": v(-225, 85) * mm, "radius": 10 * mm});
            skCircle(sketch, "E179.MirrorC", {"center": v(-75, 85) * mm, "radius": 10 * mm});
            skCircle(sketch, "E180.MirrorC", {"center": v(-225, 235) * mm, "radius": 10 * mm});
            skCircle(sketch, "E181.MirrorC", {"center": v(-75, 235) * mm, "radius": 10 * mm});
            skCircle(sketch, "E182.MirrorC", {"center": v(-225, 385) * mm, "radius": 10 * mm});
            skCircle(sketch, "E183.MirrorC", {"center": v(-75, 385) * mm, "radius": 10 * mm});
            skCircle(sketch, "E184.MirrorC", {"center": v(-75, 535) * mm, "radius": 10 * mm});
            skCircle(sketch, "E185.MirrorC", {"center": v(-225, 535) * mm, "radius": 10 * mm});
            skCircle(sketch, "E186.MirrorC", {"center": v(75, 535) * mm, "radius": 10 * mm});
            skCircle(sketch, "E187.MirrorC", {"center": v(225, 535) * mm, "radius": 10 * mm});
            skCircle(sketch, "E188.MirrorC", {"center": v(225, 385) * mm, "radius": 10 * mm});
            skCircle(sketch, "E189.MirrorC", {"center": v(75, 385) * mm, "radius": 10 * mm});
            skCircle(sketch, "E190.MirrorC", {"center": v(225, 235) * mm, "radius": 10 * mm});
            skCircle(sketch, "E191.MirrorC", {"center": v(75, 235) * mm, "radius": 10 * mm});
            skCircle(sketch, "E192.MirrorC", {"center": v(75, 85) * mm, "radius": 10 * mm});
            skCircle(sketch, "E193.MirrorC", {"center": v(225, 85) * mm, "radius": 10 * mm});
            skSolve(sketch);
        }
        {
            var Q0;
            Q0 = qSketchRegion(id + "F40", true);
            extrude(context, id + "F41", {"entities" : qUnion([Q0]), "operationType" : NewBodyOperationType.REMOVE, "oppositeDirection" : true, "depth" : 10 * mm, "offsetDistance" : 25 * mm});
        }
        {
            var Q0;
            Q0=makeQuery(id+"F1.opExtrude","SWEPT_FACE",FACE,{"disambiguationData":[OSD([sQuery(id+"F0.wireOp",EDGE,"E0.left")])]});
            var sketch = newSketch(context, id + "F42", { "sketchPlane" : qUnion([Q0])});
            skCircle(sketch, "E194", {"center": v(-235, 75) * mm, "radius": 25 * mm});
            skSolve(sketch);
        }
        {
            var Q0;
            Q0 = qSketchRegion(id + "F42", true);
            extrude(context, id + "F43", {"entities" : qUnion([Q0]), "operationType" : NewBodyOperationType.REMOVE, "oppositeDirection" : true, "depth" : 10 * mm, "offsetDistance" : 25 * mm});
        }
        {
            var Q0;
            Q0=makeQuery(id+"F34.opExtrude","CAP_FACE",FACE,{"disambiguationData":[OSD([sQuery(id+"F33.wireOp",EDGE,"E150.bottom"),sQuery(id+"F33.wireOp",EDGE,"E150.top"),sQuery(id+"F33.wireOp",EDGE,"E150.left"),sQuery(id+"F33.wireOp",EDGE,"E150.right"),sQuery(id+"F33.wireOp",EDGE,"E151"),sQuery(id+"F33.wireOp",EDGE,"E152"),sQuery(id+"F33.wireOp",EDGE,"E153"),sQuery(id+"F33.wireOp",EDGE,"E154"),sQuery(id+"F33.wireOp",EDGE,"E155"),sQuery(id+"F33.wireOp",EDGE,"E156"),sQuery(id+"F33.wireOp",EDGE,"E157"),sQuery(id+"F33.wireOp",EDGE,"E158"),sQuery(id+"F33.wireOp",EDGE,"E159"),sQuery(id+"F33.wireOp",EDGE,"E160"),sQuery(id+"F33.wireOp",EDGE,"E161"),sQuery(id+"F33.wireOp",EDGE,"E162")])],"isStart":false});
            var sketch = newSketch(context, id + "F44", { "sketchPlane" : qUnion([Q0])});
            skCircle(sketch, "E195", {"center": v(-405, -240) * mm, "radius": 25 * mm});
            skCircle(sketch, "E196", {"center": v(-405, -240) * mm, "radius": 40 * mm});
            skSolve(sketch);
        }
        {
            var Q0;
            Q0 = qSketchRegion(id + "F44", true);
            extrude(context, id + "F45", {"entities" : qUnion([Q0]), "operationType" : NewBodyOperationType.ADD, "depth" : 20 * mm, "offsetDistance" : 25 * mm});
        }
    });
